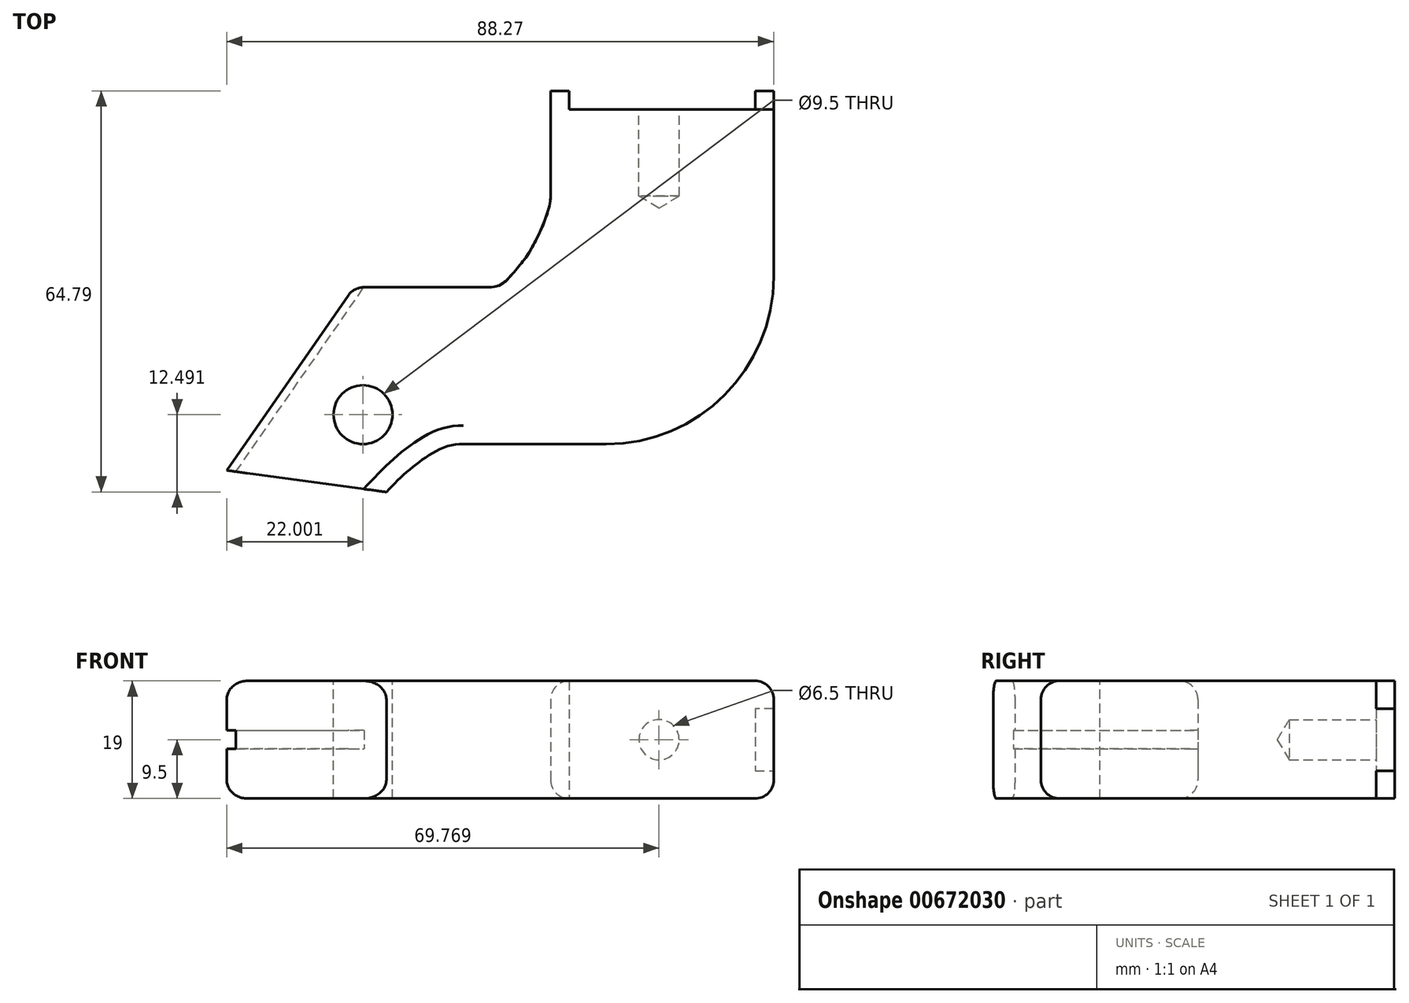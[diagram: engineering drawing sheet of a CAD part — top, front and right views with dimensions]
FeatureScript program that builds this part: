
annotation { "Feature Type Name" : "Feature", "Feature Type Description" : "" }
export const myFeature = defineFeature(function(context is Context, id is Id, definition is map)
    precondition{}
    {
        {
            var Q0;
            Q0=qCreatedBy(makeId("Top.planeOp"),FACE);
            var sketch = newSketch(context, id + "F0", { "sketchPlane" : qUnion([Q0])});
            skLineSegment(sketch, "E0", {"start": v(26.3, 4.36) * mm, "end": v(56.3, 4.36) * mm});
            skLineSegment(sketch, "E1", {"start": v(56.3, 4.36) * mm, "end": v(56.3, 7.36) * mm});
            skLineSegment(sketch, "E2", {"start": v(26.3, 4.36) * mm, "end": v(26.3, 7.36) * mm});
            skLineSegment(sketch, "E3", {"start": v(26.3, 7.36) * mm, "end": v(23.3, 7.36) * mm});
            skLineSegment(sketch, "E4", {"start": v(56.3, 7.36) * mm, "end": v(59.3, 7.36) * mm});
            skLineSegment(sketch, "E5", {"start": v(59.3, 7.36) * mm, "end": v(59.3, -22.64) * mm});
            skLineSegment(sketch, "E6", {"start": v(9.23, -49.7) * mm, "end": v(32.23, -49.7) * mm});
            skArc(sketch, "E7", {"start": v(59.3, -22.64) * mm, "mid": v(51.37, -41.78) * mm, "end": v(32.23, -49.7) * mm});
            skFitSpline(sketch, "E8", {"points": [v(9.23, -49.7) * mm, v(6, -50.26) * mm, v(0.56, -53.8) * mm, v(-3.2, -57.43) * mm], "startDerivative": vector(-11.14, 0) * mm, "endDerivative": vector(-9.92, -10.35) * mm});
            skLineSegment(sketch, "E9", {"start": v(-3.2, -57.43) * mm, "end": v(-28.97, -53.94) * mm});
            skLineSegment(sketch, "E10", {"start": v(-28.97, -53.94) * mm, "end": v(-9.34, -25.67) * mm});
            skLineSegment(sketch, "E11", {"start": v(-6.88, -24.38) * mm, "end": v(13.36, -24.38) * mm});
            skPoint(sketch, "E12.visualSharp", {"position": v(-8.45, -24.38) * mm});
            skArc(sketch, "E12.filletArc", {"start": v(-6.88, -24.38) * mm, "mid": v(-8.27, -24.72) * mm, "end": v(-9.34, -25.67) * mm});
            skLineSegment(sketch, "E13", {"start": v(23.3, 7.36) * mm, "end": v(23.3, -9.64) * mm});
            skFitSpline(sketch, "E14", {"points": [v(23.3, -9.64) * mm, v(19.87, -18.68) * mm, v(18.14, -21) * mm, v(15.68, -23.65) * mm, v(13.36, -24.38) * mm], "startDerivative": vector(0, -20.49) * mm, "endDerivative": vector(-13.4, 0) * mm});
            skSolve(sketch);
        }
        {
            var Q0;
            Q0=makeQuery(id+"F0.imprint","IMPRINT",FACE,{"disambiguationData":[TD([[makeQuery(id+"F0.imprint","IMPRINT",EDGE,{"derivedFrom":sQuery(id+"F0.wireOp",EDGE,"E0")}),-1.0]])]});
            extrude(context, id + "F1", {"entities" : qUnion([Q0]), "depth" : 19 * mm, "offsetDistance" : 25 * mm});
        }
        {
            var Q0;
            Q0=makeQuery(id+"F1.opExtrude","CAP_FACE",FACE,{"disambiguationData":[OSD([sQuery(id+"F0.wireOp",EDGE,"E0"),sQuery(id+"F0.wireOp",EDGE,"E1"),sQuery(id+"F0.wireOp",EDGE,"E2"),sQuery(id+"F0.wireOp",EDGE,"E3"),sQuery(id+"F0.wireOp",EDGE,"E4"),sQuery(id+"F0.wireOp",EDGE,"E5"),sQuery(id+"F0.wireOp",EDGE,"E6"),sQuery(id+"F0.wireOp",EDGE,"E7"),sQuery(id+"F0.wireOp",EDGE,"E8"),sQuery(id+"F0.wireOp",EDGE,"E9"),sQuery(id+"F0.wireOp",EDGE,"E10"),sQuery(id+"F0.wireOp",EDGE,"E11"),sQuery(id+"F0.wireOp",EDGE,"E12.filletArc"),sQuery(id+"F0.wireOp",EDGE,"E13"),sQuery(id+"F0.wireOp",EDGE,"E14")])],"isStart":true});
            var sketch = newSketch(context, id + "F2", { "sketchPlane" : qUnion([Q0])});
            skLineSegment(sketch, "E15.0", {"start": v(-28.97, 53.94) * mm, "end": v(0.21, 11.91) * mm});
            skPoint(sketch, "E16.orphan", {"position": v(-9.34, 25.67) * mm});
            skSolve(sketch);
        }
        {
            var Q0;
            Q0=makeQuery(id+"F1.opExtrude","SWEPT_FACE",FACE,{"disambiguationData":[OSD([sQuery(id+"F0.wireOp",EDGE,"E9")])]});
            var sketch = newSketch(context, id + "F3", { "sketchPlane" : qUnion([Q0])});
            skLineSegment(sketch, "E17.bottom", {"start": v(-22.96, 11) * mm, "end": v(-19.96, 11) * mm});
            skLineSegment(sketch, "E17.top", {"start": v(-22.96, 8) * mm, "end": v(-19.96, 8) * mm});
            skLineSegment(sketch, "E17.left", {"start": v(-22.96, 11) * mm, "end": v(-22.96, 8) * mm});
            skLineSegment(sketch, "E17.right", {"start": v(-19.96, 11) * mm, "end": v(-19.96, 8) * mm});
            skPoint(sketch, "E17.middle", {"position": v(-21.46, 9.5) * mm});
            skSolve(sketch);
        }
        {
            var Q0;
            Q0 = qSketchRegion(id + "F3", true);
            var Q1;
            Q1=sQuery(id+"F2.wireOp",EDGE,"E15.0");
            sweep(context, id + "F4", {"operationType" : NewBodyOperationType.REMOVE, "profiles" : qUnion([Q0]), "path" : qUnion([Q1])});
        }
        {
            var Q0;
            Q0=makeQuery(id+"F1.opExtrude","CAP_FACE",FACE,{"disambiguationData":[OSD([sQuery(id+"F0.wireOp",EDGE,"E0"),sQuery(id+"F0.wireOp",EDGE,"E1"),sQuery(id+"F0.wireOp",EDGE,"E2"),sQuery(id+"F0.wireOp",EDGE,"E3"),sQuery(id+"F0.wireOp",EDGE,"E4"),sQuery(id+"F0.wireOp",EDGE,"E5"),sQuery(id+"F0.wireOp",EDGE,"E6"),sQuery(id+"F0.wireOp",EDGE,"E7"),sQuery(id+"F0.wireOp",EDGE,"E8"),sQuery(id+"F0.wireOp",EDGE,"E9"),sQuery(id+"F0.wireOp",EDGE,"E10"),sQuery(id+"F0.wireOp",EDGE,"E11"),sQuery(id+"F0.wireOp",EDGE,"E12.filletArc"),sQuery(id+"F0.wireOp",EDGE,"E13"),sQuery(id+"F0.wireOp",EDGE,"E14")])],"isStart":false});
            var sketch = newSketch(context, id + "F5", { "sketchPlane" : qUnion([Q0])});
            skCircle(sketch, "E18", {"center": v(-6.97, -44.94) * mm, "radius": 4.75 * mm});
            skSolve(sketch);
        }
        {
            var Q0;
            Q0=sQuery(id+"F5.wireOp",VERTEX,"E18.center");
            var Q1;
            Q1=makeQuery(id+"F1.opExtrude","SWEPT_BODY",BODY,{"disambiguationData":[OSD([sQuery(id+"F0.wireOp",EDGE,"E0"),sQuery(id+"F0.wireOp",EDGE,"E1"),sQuery(id+"F0.wireOp",EDGE,"E2"),sQuery(id+"F0.wireOp",EDGE,"E3"),sQuery(id+"F0.wireOp",EDGE,"E4"),sQuery(id+"F0.wireOp",EDGE,"E5"),sQuery(id+"F0.wireOp",EDGE,"E6"),sQuery(id+"F0.wireOp",EDGE,"E7"),sQuery(id+"F0.wireOp",EDGE,"E8"),sQuery(id+"F0.wireOp",EDGE,"E9"),sQuery(id+"F0.wireOp",EDGE,"E10"),sQuery(id+"F0.wireOp",EDGE,"E11"),sQuery(id+"F0.wireOp",EDGE,"E12.filletArc"),sQuery(id+"F0.wireOp",EDGE,"E13"),sQuery(id+"F0.wireOp",EDGE,"E14")])]});
            hole(context, id + "F6", {"style" : HoleStyle.SIMPLE, "endStyle" : HoleEndStyle.THROUGH, "holeDiameter" : 9.5 * mm, "majorDiameter" : 5 * mm, "isTappedThrough" : true, "tappedDepth" : 12 * mm, "tapClearance" : 3, "locations" : qUnion([Q0]), "scope" : qUnion([Q1])});
        }
        {
            var Q0;
            Q0=makeQuery(id+"F1.opExtrude","SWEPT_FACE",FACE,{"disambiguationData":[OSD([sQuery(id+"F0.wireOp",EDGE,"E0")])]});
            var sketch = newSketch(context, id + "F7", { "sketchPlane" : qUnion([Q0])});
            skLineSegment(sketch, "E19.0.0", {"start": v(-59.3, 0) * mm, "end": v(-56.3, 0) * mm});
            skLineSegment(sketch, "E19.0.1", {"start": v(-56.3, 0) * mm, "end": v(-56.3, 4.5) * mm});
            skLineSegment(sketch, "E19.0.2", {"start": v(-56.3, 19) * mm, "end": v(-59.3, 19) * mm});
            skLineSegment(sketch, "E19.0.3", {"start": v(-59.3, 19) * mm, "end": v(-59.3, 14.5) * mm});
            skLineSegment(sketch, "E20.0", {"start": v(-56.3, 14.5) * mm, "end": v(-59.3, 14.5) * mm});
            skLineSegment(sketch, "E21.0", {"start": v(-59.3, 4.5) * mm, "end": v(-56.3, 4.5) * mm});
            skLineSegment(sketch, "E22.trimOffspring", {"start": v(-59.3, 4.5) * mm, "end": v(-59.3, 0) * mm});
            skLineSegment(sketch, "E23.trimOffspring", {"start": v(-56.3, 14.5) * mm, "end": v(-56.3, 19) * mm});
            skSolve(sketch);
        }
        {
            var Q0;
            Q0 = qSketchRegion(id + "F7", true);
            extrude(context, id + "F8", {"entities" : qUnion([Q0]), "operationType" : NewBodyOperationType.REMOVE, "depth" : 4 * mm, "offsetDistance" : 25 * mm});
        }
        {
            var Q0;
            Q0=makeQuery(id+"F8.boolean.opBoolean","MERGE",FACE,{"derivedFrom":[makeQuery(id+"F1.opExtrude","SWEPT_FACE",FACE,{"disambiguationData":[OSD([sQuery(id+"F0.wireOp",EDGE,"E0")])]}),makeQuery(id+"F8.opExtrude","CAP_FACE",FACE,{"disambiguationData":[OSD([sQuery(id+"F7.wireOp",EDGE,"E19.0.0"),sQuery(id+"F7.wireOp",EDGE,"E19.0.1"),sQuery(id+"F7.wireOp",EDGE,"E21.0"),sQuery(id+"F7.wireOp",EDGE,"E22.trimOffspring")])],"isStart":true}),makeQuery(id+"F8.opExtrude","CAP_FACE",FACE,{"disambiguationData":[OSD([sQuery(id+"F7.wireOp",EDGE,"E19.0.2"),sQuery(id+"F7.wireOp",EDGE,"E19.0.3"),sQuery(id+"F7.wireOp",EDGE,"E20.0"),sQuery(id+"F7.wireOp",EDGE,"E23.trimOffspring")])],"isStart":true})]});
            var sketch = newSketch(context, id + "F9", { "sketchPlane" : qUnion([Q0])});
            skCircle(sketch, "E24", {"center": v(-40.8, 9.5) * mm, "radius": 3.13 * mm});
            skPoint(sketch, "E24.centerSnap0", {"position": v(-56.3, 9.5) * mm});
            skSolve(sketch);
        }
        {
            var Q0;
            Q0=sQuery(id+"F9.wireOp",VERTEX,"E24.center");
            var Q1;
            Q1=makeQuery(id+"F1.opExtrude","SWEPT_BODY",BODY,{"disambiguationData":[OSD([sQuery(id+"F0.wireOp",EDGE,"E0"),sQuery(id+"F0.wireOp",EDGE,"E1"),sQuery(id+"F0.wireOp",EDGE,"E2"),sQuery(id+"F0.wireOp",EDGE,"E3"),sQuery(id+"F0.wireOp",EDGE,"E4"),sQuery(id+"F0.wireOp",EDGE,"E5"),sQuery(id+"F0.wireOp",EDGE,"E6"),sQuery(id+"F0.wireOp",EDGE,"E7"),sQuery(id+"F0.wireOp",EDGE,"E8"),sQuery(id+"F0.wireOp",EDGE,"E9"),sQuery(id+"F0.wireOp",EDGE,"E10"),sQuery(id+"F0.wireOp",EDGE,"E11"),sQuery(id+"F0.wireOp",EDGE,"E12.filletArc"),sQuery(id+"F0.wireOp",EDGE,"E13"),sQuery(id+"F0.wireOp",EDGE,"E14")])]});
            hole(context, id + "F10", {"style" : HoleStyle.SIMPLE, "endStyle" : HoleEndStyle.BLIND, "holeDiameter" : 6.5 * mm, "majorDiameter" : 5 * mm, "holeDepth" : 14 * mm, "isTappedThrough" : true, "tappedDepth" : 12 * mm, "tapClearance" : 3, "locations" : qUnion([Q0]), "scope" : qUnion([Q1])});
        }
        {
            var Q0;
            Q0=makeQuery(id+"F1.opExtrude","CAP_EDGE",EDGE,{"disambiguationData":[OSD([sQuery(id+"F0.wireOp",EDGE,"E13")])],"isStart":false});
            var Q1;
            Q1=makeQuery(id+"F1.opExtrude","CAP_EDGE",EDGE,{"disambiguationData":[OSD([sQuery(id+"F0.wireOp",EDGE,"E13")])],"isStart":true});
            var Q2;
            Q2=makeQuery(id+"F1.opExtrude","CAP_EDGE",EDGE,{"disambiguationData":[OSD([sQuery(id+"F0.wireOp",EDGE,"E8")])],"isStart":true});
            var Q3;
            Q3=makeQuery(id+"F1.opExtrude","CAP_EDGE",EDGE,{"disambiguationData":[OSD([sQuery(id+"F0.wireOp",EDGE,"E8")])],"isStart":false});
            fillet(context, id + "F11", {"entities" : qUnion([Q0, Q1, Q2, Q3]), "radius" : 3 * mm, "tangentPropagation" : true, "allowEdgeOverflow" : false});
        }
    });
